# Revit family: Dartmouth Single GU10
name_source: partatom
category: Lighting Fixtures
revit_build: Autodesk Revit 2018 (Build: 20170223_1515(x64)
units: mm (PartAtom-declared; Revit-internal decimal feet)

## family parameters
Always vertical = Yes
Cut with Voids When Loaded = No
Host = Wall
Light Source = No
OmniClass Number = 23.80.70.00
OmniClass Title = Lighting
Part Type = Normal
Room Calculation Point = No
Round Connector Dimension = Use Diameter
Shared = No

## types (3) — shared parameters
Dimensions MM = 98 x 65 x 96
Dimmable = Lamp Dependent
Dimming Method = Lamp Dependent
Driver Required = No
Efficacy (lm/w) = Lamp Dependent
Electrical Class = 1
Lamp = GU 10 LED
Location rating = IP54
Main Material = Metal - Aluminium
Manufacturer = Astro Lighting Ltd
Power (Watts) = 6 W Max
Product Location = Outdoor, Zone 2, 3
Product Name = Dartmouth Single
Product URL = https://www.astrolighting.com
URL = www.astrolighting.com
Weight KG = 0.5

## per-type parameters (varying)
| type | Main Finish | Product SKU |
| Astro Dartmouth Single Textured White | Textured White | 1372009 |
| Astro Dartmouth Single Textured Grey | Textured Grey | 1372010 |
| Astro Dartmouth Single Textured Black | Textured Black
Textured Black | 1372011 |

## geometry (parser evidence)
native form markers: Sweep x2
no freeform markers — native parametric forms only
